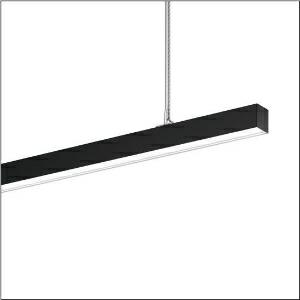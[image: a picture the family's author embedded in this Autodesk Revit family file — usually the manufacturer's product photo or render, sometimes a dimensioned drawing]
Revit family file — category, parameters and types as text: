
# Revit family: silica_r__21_51mx33tbt9b_b685
name_source: partatom
category: Lighting Fixtures
units: mm (PartAtom-declared; Revit-internal decimal feet)

## family parameters
Cut with Voids When Loaded = No
Host = Face
Light Source = No
Part Type = Normal
Room Calculation Point = No
Round Connector Dimension = Use Diameter
Shared = No

## types (1)
- --- (1 x LED, 7170 lm, 67.4 W, 6500K)
    Apparent Load = 67 VA
    CIE Flux Codes = 78 96 99 56 100
    Color Rendering = 80
    Color Temperature = 6500K
    Default Elevation = 1800 mm
    Description = Silica® 21, office luminaire, primary optical cover: prismatic diffuser, of PMMA, CAT 2 (L<= 3000cd/m²), light emission: direct/indirect distribution, primary light characteristic: symmetric, installation type: suspended mounting, LED, rated luminous flux: 7.170lm, luminous efficacy: 101lm/W, light colour: 8tw, colour temperature: 2700..6500K, control gear: ECG DALI, with terminal, 3+2-pole, max. 2.5mm², mains connection: 220..240V, AC, 50/60Hz, rated input power: 70.8W, luminaire housing, of aluminium, jet black (RAL 9005), length: 1.504mm, width: 53mm, height: 53mm, protection rating (complete): IP20, insulation class (complete): insulation class I (protective earthing), certification: CE, permissible operating ambient temperature: 0..+35°C, standard: EN 50419, packaging unit: 1 piece
    Height = 53 mm
    Lamp = 1 x LED
    Lamp Light Flux = 7170 lm
    Lamp Power = 67.4 W
    Lamp count = 1
    Length = 1504 mm
    Luminous efficacy = 106 lm/W
    Manufacturer = Siteco
    ModVariant = No
    Model = 51MX33TBT9B
    Mounting Place = Ceiling
    Mounting Type = Pendant
    Number of Poles = 1
    OnlyDefault = Yes
    Power Factor = 1
    Product Name = Silica® 21
    Product group = office luminaire | ceiling pendant
    ProductGroupID = 905
    Protection Class = Protection class I
    Protection Degree = IP 20
    RLX_Detail_Level = 1
    RlxData = <blob elided: 22953 chars, md5=8b8b88c4>
    Socket = socket
    Standby Power = 0 W
    System Light Flux = 7170 lm
    System Power = 67 W
    Type Comments = individual setting
    Type Image = l_1251735.jpg
    URL = http://relux.com
    VarID = @adj_045849
    Voltage = 0 V
    Weight = 0.00 kg
    Width = 53 mm

## geometry (parser evidence)
native form markers: Blend x4, Sweep x13
no freeform markers — native parametric forms only
